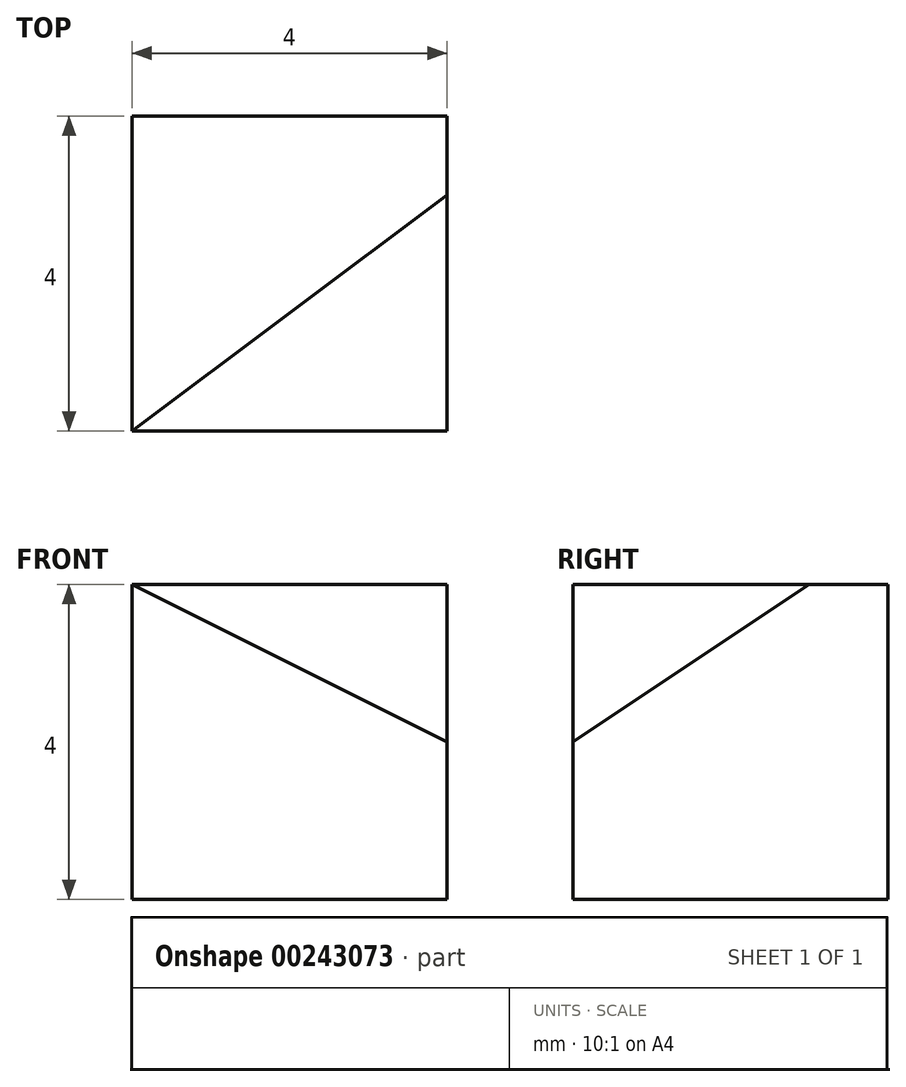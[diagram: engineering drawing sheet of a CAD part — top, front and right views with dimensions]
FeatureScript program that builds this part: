
annotation { "Feature Type Name" : "Feature", "Feature Type Description" : "" }
export const myFeature = defineFeature(function(context is Context, id is Id, definition is map)
    precondition{}
    {
        {
            var Q0;
            Q0=qCreatedBy(makeId("Top.planeOp"),FACE);
            var sketch = newSketch(context, id + "F0", { "sketchPlane" : qUnion([Q0])});
            skLineSegment(sketch, "E0.bottom", {"start": v(0, 0) * mm, "end": v(4, 0) * mm});
            skLineSegment(sketch, "E0.top", {"start": v(0, 4) * mm, "end": v(4, 4) * mm});
            skLineSegment(sketch, "E0.left", {"start": v(0, 0) * mm, "end": v(0, 4) * mm});
            skLineSegment(sketch, "E0.right", {"start": v(4, 0) * mm, "end": v(4, 4) * mm});
            skSolve(sketch);
        }
        {
            var Q0;
            Q0 = qSketchRegion(id + "F0", true);
            var Q1;
            Q1=makeQuery(id+"F0.imprint","IMPRINT",FACE,{"disambiguationData":[TD([[makeQuery(id+"F0.imprint","IMPRINT",EDGE,{"derivedFrom":sQuery(id+"F0.wireOp",EDGE,"E0.bottom")}),1.0]])]});
            extrude(context, id + "F1", {"entities" : qUnion([Q0, Q1]), "depth" : 4 * mm});
        }
        {
            var Q0;
            Q0=makeQuery(id+"F1.opExtrude","SWEPT_FACE",FACE,{"disambiguationData":[OSD([sQuery(id+"F0.wireOp",EDGE,"E0.right")])]});
            var sketch = newSketch(context, id + "F2", { "sketchPlane" : qUnion([Q0])});
            skLineSegment(sketch, "E1", {"start": v(4, 4) * mm, "end": v(3, 4) * mm});
            skLineSegment(sketch, "E2", {"start": v(0, 0) * mm, "end": v(0, 2) * mm});
            skSolve(sketch);
        }
        {
            var Q0;
            Q0=sQuery(id+"F2.wireOp",VERTEX,"E1.end");
            var Q1;
            Q1=sQuery(id+"F2.wireOp",VERTEX,"E2.end");
            var Q2;
            Q2=makeQuery(id+"F1.opExtrude","CAP_VERTEX",VERTEX,{"disambiguationData":[OSD([sQuery(id+"F0.wireOp",EDGE,"E0.bottom"),sQuery(id+"F0.wireOp",EDGE,"E0.left")])],"isStart":false});
            cPlane(context, id + "F3", {"entities" : qUnion([Q0, Q1, Q2]), "cplaneType" : CPlaneType.THREE_POINT, "offset" : 25 * mm, "width" : 150 * mm, "height" : 150 * mm});
        }
        {
            var Q0;
            Q0=qCreatedBy(id+"F3.planeOp",FACE);
            var sketch = newSketch(context, id + "F4", { "sketchPlane" : qUnion([Q0])});
            skPoint(sketch, "E3.0", {"position": v(-1.28, 2.22) * mm});
            skPoint(sketch, "E3.1", {"position": v(3.05, 4.71) * mm});
            skPoint(sketch, "E3.2", {"position": v(3.05, 1.1) * mm});
            skLineSegment(sketch, "E4", {"start": v(-1.28, 2.22) * mm, "end": v(3.05, 1.1) * mm});
            skLineSegment(sketch, "E5", {"start": v(3.05, 4.71) * mm, "end": v(3.05, 1.1) * mm});
            skLineSegment(sketch, "E6", {"start": v(3.05, 4.71) * mm, "end": v(-1.28, 2.22) * mm});
            skSolve(sketch);
        }
        {
            var Q0;
            Q0 = qSketchRegion(id + "F4", true);
            extrude(context, id + "F5", {"entities" : qUnion([Q0]), "operationType" : NewBodyOperationType.REMOVE, "depth" : 25 * mm});
        }
    });
